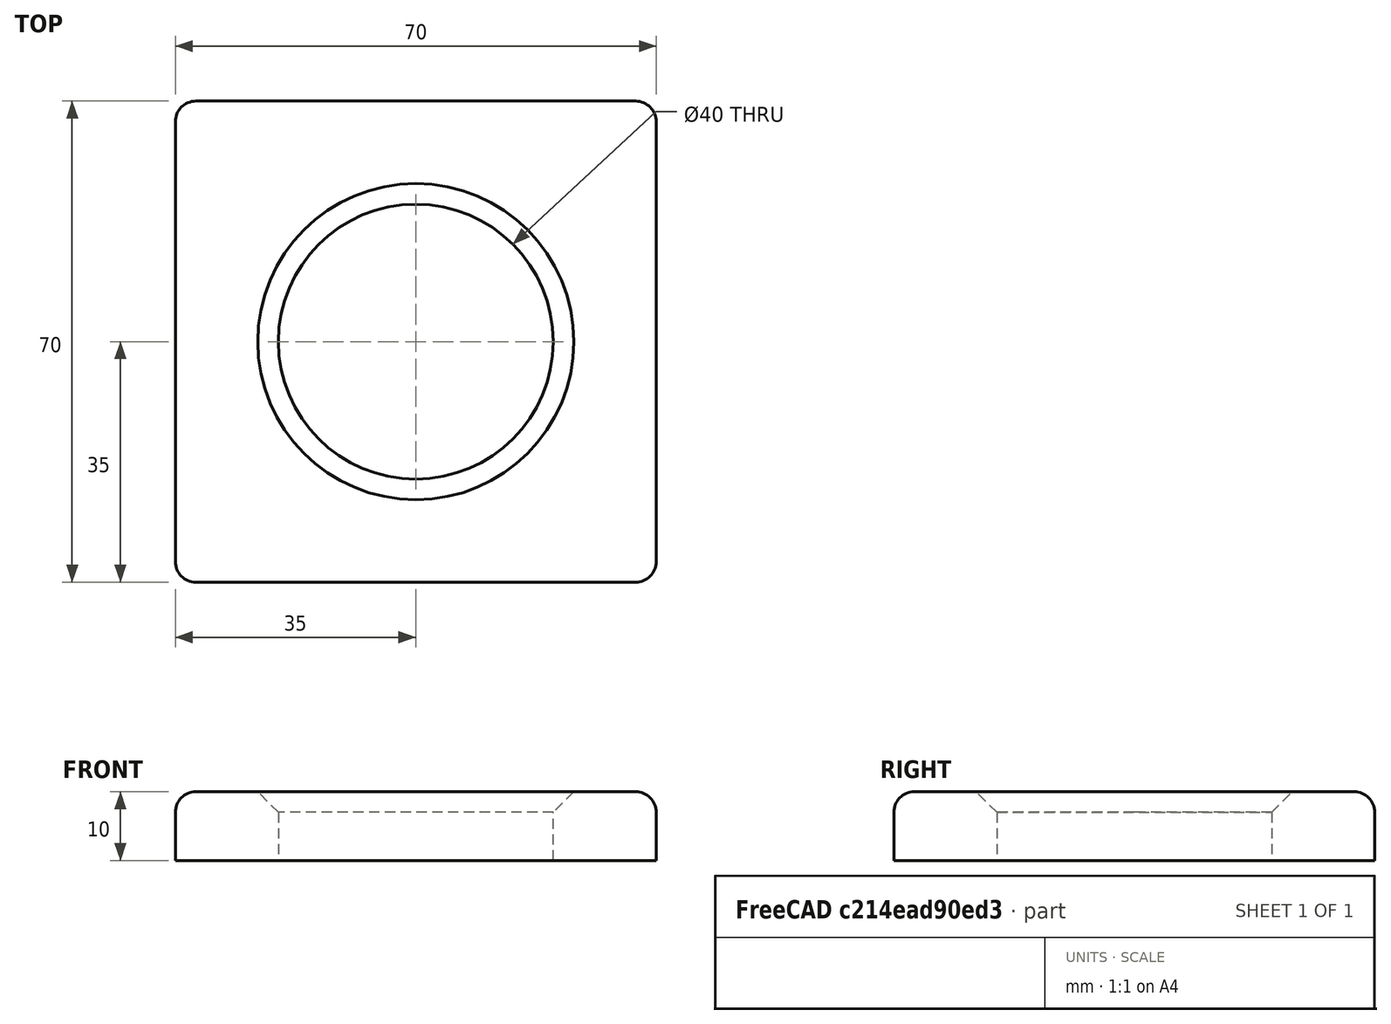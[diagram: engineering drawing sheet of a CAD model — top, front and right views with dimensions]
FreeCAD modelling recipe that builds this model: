
FCSTD DOCUMENT  (FreeCAD 1.0R39319 (Git))
Label: globe-stand
License: All rights reserved
LicenseURL: https://en.wikipedia.org/wiki/All_rights_reserved
objects: Part::Box×1, Part::Cylinder×1, Part::Cut×1, Part::Chamfer×1, Part::Fillet×1
note: 5 computed .brp shape members not serialized (recipe doc carries the construction recipe); baked Part::Feature solids carry a one-line shape summary decoded from their .brp

FEATURE [Part::Box] Box
  AttacherType = Attacher::AttachEngine3D
  Height = 10
  Length = 70
  Placement = pos=(-35,-35,0) rot=(0,0,1;0rad)
  Width = 70
FEATURE [Part::Cylinder] Cylinder
  Angle = 360
  AttacherType = Attacher::AttachEngine3D
  FirstAngle = 0
  Height = 20
  Placement = pos=(0,0,-1) rot=(0,0,1;0rad)
  Radius = 20
  SecondAngle = 0
FEATURE [Part::Cut] Cut
  Base = -> Box
  Refine = true
  Tool = -> Cylinder
FEATURE [Part::Chamfer] Chamfer
  Base = -> Cut
  EdgeLinks = -> Cut [Edge10]
  Edges = 1 edges r=3: [Edge10]
FEATURE [Part::Fillet] Fillet
  Base = -> Chamfer
  EdgeLinks = -> Chamfer [Edge2,Edge3,Edge4,Edge5,Edge8,Edge9,Edge12,Edge14]
  Edges = 8 edges r=3: [Edge2,Edge3,Edge4,Edge5,Edge8,Edge9,Edge12,Edge14]
